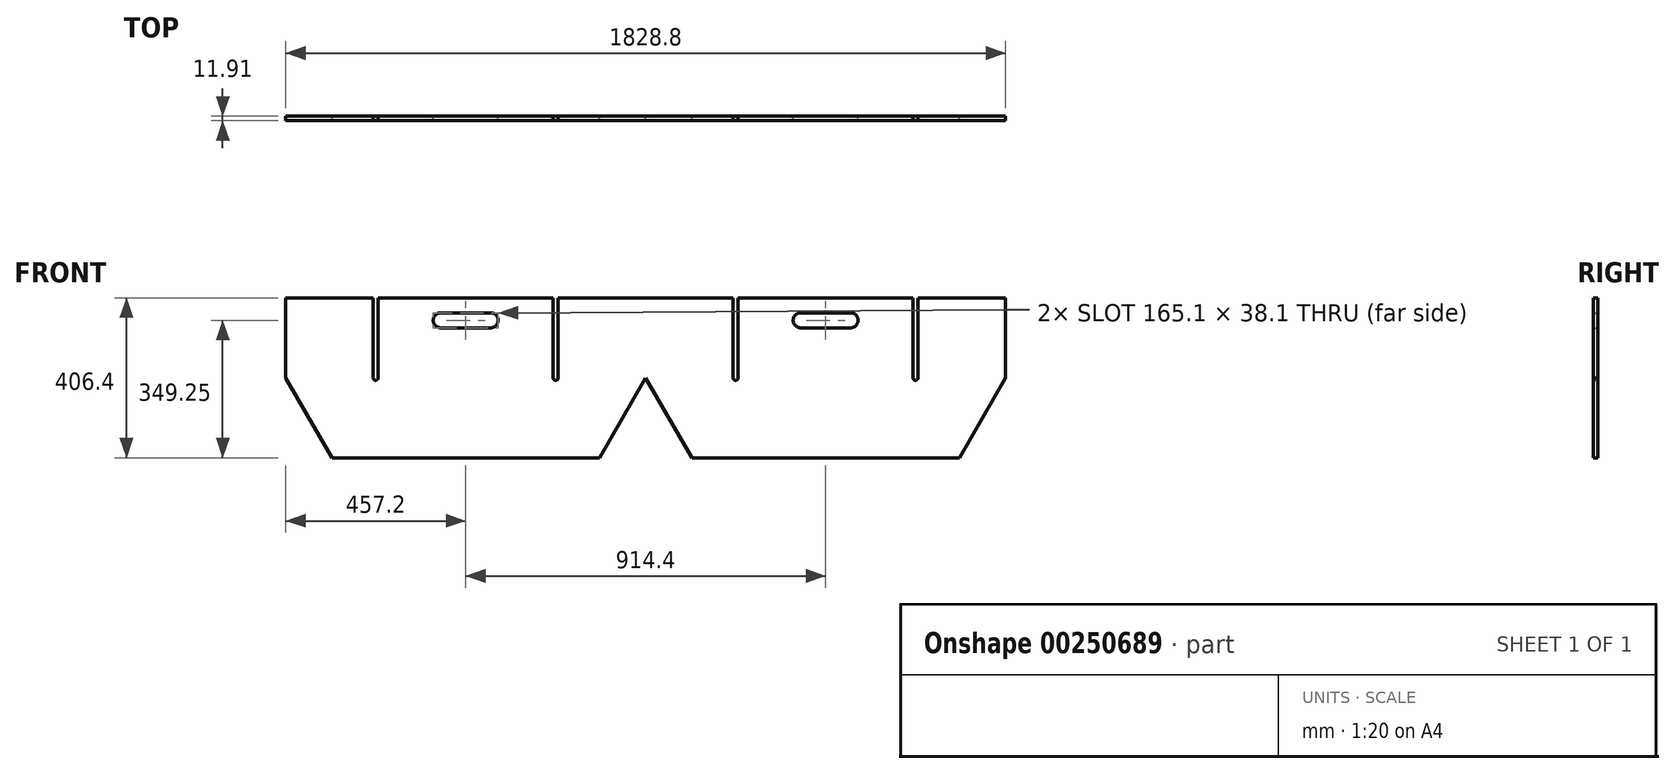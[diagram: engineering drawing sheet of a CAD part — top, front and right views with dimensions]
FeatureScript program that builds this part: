
annotation { "Feature Type Name" : "Feature", "Feature Type Description" : "" }
export const myFeature = defineFeature(function(context is Context, id is Id, definition is map)
    precondition{}
    {
        {
            var Q0;
            Q0=qCreatedBy(makeId("Front.planeOp"),FACE);
            var sketch = newSketch(context, id + "F0", { "sketchPlane" : qUnion([Q0])});
            skLineSegment(sketch, "E0.bottom", {"start": v(117.32, 0) * mm, "end": v(797.08, 0) * mm});
            skLineSegment(sketch, "E0.top", {"start": v(0, 406.4) * mm, "end": v(222.25, 406.4) * mm});
            skLineSegment(sketch, "E0.left", {"start": v(0, 203.2) * mm, "end": v(0, 406.4) * mm});
            skLineSegment(sketch, "E0.right", {"start": v(914.4, 0) * mm, "end": v(914.4, 406.4) * mm, "construction": true});
            skLineSegment(sketch, "E1", {"start": v(0, 203.2) * mm, "end": v(117.32, 0) * mm});
            skLineSegment(sketch, "E2", {"start": v(914.4, 203.2) * mm, "end": v(797.08, 0) * mm});
            skPoint(sketch, "E3.orphan", {"position": v(0, 0) * mm});
            skPoint(sketch, "E4", {"position": v(228.6, 406.4) * mm});
            skPoint(sketch, "E5", {"position": v(685.8, 406.4) * mm});
            skLineSegment(sketch, "E6", {"start": v(228.6, 406.4) * mm, "end": v(228.6, 203.2) * mm, "construction": true});
            skLineSegment(sketch, "E7", {"start": v(685.8, 406.4) * mm, "end": v(685.8, 203.2) * mm, "construction": true});
            skArc(sketch, "E8", {"start": v(222.25, 203.2) * mm, "mid": v(228.6, 196.85) * mm, "end": v(234.95, 203.2) * mm});
            skArc(sketch, "E9", {"start": v(679.45, 203.2) * mm, "mid": v(686.64, 196.9) * mm, "end": v(691.93, 204.87) * mm});
            skLineSegment(sketch, "E10", {"start": v(222.25, 203.2) * mm, "end": v(222.25, 406.4) * mm});
            skLineSegment(sketch, "E11", {"start": v(234.95, 203.2) * mm, "end": v(234.95, 406.4) * mm});
            skLineSegment(sketch, "E12", {"start": v(679.45, 203.2) * mm, "end": v(679.45, 406.4) * mm});
            skLineSegment(sketch, "E13", {"start": v(691.93, 204.87) * mm, "end": v(691.93, 406.4) * mm});
            skLineSegment(sketch, "E14.trimOffspring", {"start": v(691.93, 406.4) * mm, "end": v(914.4, 406.4) * mm});
            skLineSegment(sketch, "E15.trimOffspring", {"start": v(234.95, 406.4) * mm, "end": v(679.45, 406.4) * mm});
            skLineSegment(sketch, "E16", {"start": v(457.2, 406.4) * mm, "end": v(457.2, 368.3) * mm, "construction": true});
            skLineSegment(sketch, "E17", {"start": v(457.2, 368.3) * mm, "end": v(457.2, 330.2) * mm, "construction": true});
            skLineSegment(sketch, "E18", {"start": v(457.2, 368.3) * mm, "end": v(393.7, 368.3) * mm});
            skLineSegment(sketch, "E19", {"start": v(457.2, 330.2) * mm, "end": v(393.7, 330.2) * mm});
            skArc(sketch, "E20", {"start": v(393.7, 368.3) * mm, "mid": v(374.65, 349.25) * mm, "end": v(393.7, 330.2) * mm});
            skLineSegment(sketch, "E21.MirrorCS", {"start": v(457.2, 330.2) * mm, "end": v(520.7, 330.2) * mm});
            skArc(sketch, "E22.MirrorCS", {"start": v(520.7, 368.3) * mm, "mid": v(539.75, 349.25) * mm, "end": v(520.7, 330.2) * mm});
            skLineSegment(sketch, "E23.MirrorCS", {"start": v(457.2, 368.3) * mm, "end": v(520.7, 368.3) * mm});
            skArc(sketch, "E24.MirrorCS", {"start": v(1606.55, 203.2) * mm, "mid": v(1600.2, 196.85) * mm, "end": v(1593.85, 203.2) * mm});
            skArc(sketch, "E25.MirrorCS", {"start": v(1149.35, 203.2) * mm, "mid": v(1142.16, 196.9) * mm, "end": v(1136.87, 204.87) * mm});
            skLineSegment(sketch, "E26.MirrorCS", {"start": v(1371.6, 406.4) * mm, "end": v(1371.6, 368.3) * mm, "construction": true});
            skLineSegment(sketch, "E27.MirrorCS", {"start": v(1371.6, 368.3) * mm, "end": v(1435.1, 368.3) * mm});
            skLineSegment(sketch, "E28.MirrorCS", {"start": v(914.4, 203.2) * mm, "end": v(1031.72, 0) * mm});
            skPoint(sketch, "E29.MirrorP", {"position": v(1828.8, 0) * mm});
            skPoint(sketch, "E30.MirrorP", {"position": v(1143, 406.4) * mm});
            skLineSegment(sketch, "E31.MirrorCS", {"start": v(1828.8, 203.2) * mm, "end": v(1711.48, 0) * mm});
            skArc(sketch, "E32.MirrorCS", {"start": v(1308.1, 368.3) * mm, "mid": v(1289.05, 349.25) * mm, "end": v(1308.1, 330.2) * mm});
            skArc(sketch, "E33.MirrorCS", {"start": v(1435.1, 368.3) * mm, "mid": v(1454.15, 349.25) * mm, "end": v(1435.1, 330.2) * mm});
            skLineSegment(sketch, "E34.MirrorCS", {"start": v(1600.2, 406.4) * mm, "end": v(1600.2, 203.2) * mm, "construction": true});
            skPoint(sketch, "E35.MirrorP", {"position": v(1600.2, 406.4) * mm});
            skLineSegment(sketch, "E36.MirrorCS", {"start": v(1828.8, 406.4) * mm, "end": v(1606.55, 406.4) * mm});
            skLineSegment(sketch, "E37.MirrorCS", {"start": v(1711.48, 0) * mm, "end": v(1031.72, 0) * mm});
            skLineSegment(sketch, "E38.MirrorCS", {"start": v(1593.85, 203.2) * mm, "end": v(1593.85, 406.4) * mm});
            skLineSegment(sketch, "E39.MirrorCS", {"start": v(1143, 406.4) * mm, "end": v(1143, 203.2) * mm, "construction": true});
            skLineSegment(sketch, "E40.MirrorCS", {"start": v(1149.35, 203.2) * mm, "end": v(1149.35, 406.4) * mm});
            skLineSegment(sketch, "E41.MirrorCS", {"start": v(1828.8, 203.2) * mm, "end": v(1828.8, 406.4) * mm});
            skLineSegment(sketch, "E42.MirrorCS", {"start": v(1606.55, 203.2) * mm, "end": v(1606.55, 406.4) * mm});
            skLineSegment(sketch, "E43.MirrorCS", {"start": v(1371.6, 368.3) * mm, "end": v(1308.1, 368.3) * mm});
            skLineSegment(sketch, "E44.MirrorCS", {"start": v(1371.6, 330.2) * mm, "end": v(1308.1, 330.2) * mm});
            skLineSegment(sketch, "E45.MirrorCS", {"start": v(1593.85, 406.4) * mm, "end": v(1149.35, 406.4) * mm});
            skLineSegment(sketch, "E46.MirrorCS", {"start": v(1136.87, 406.4) * mm, "end": v(914.4, 406.4) * mm});
            skLineSegment(sketch, "E47.MirrorCS", {"start": v(1371.6, 368.3) * mm, "end": v(1371.6, 330.2) * mm, "construction": true});
            skLineSegment(sketch, "E48.MirrorCS", {"start": v(1136.87, 204.87) * mm, "end": v(1136.87, 406.4) * mm});
            skLineSegment(sketch, "E49.MirrorCS", {"start": v(1371.6, 330.2) * mm, "end": v(1435.1, 330.2) * mm});
            skSolve(sketch);
        }
        {
            var Q0;
            Q0=makeQuery(id+"F0.imprint","IMPRINT",FACE,{"disambiguationData":[TD([[makeQuery(id+"F0.imprint","IMPRINT",EDGE,{"derivedFrom":sQuery(id+"F0.wireOp",EDGE,"E0.bottom")}),1.0]])]});
            extrude(context, id + "F1", {"entities" : qUnion([Q0]), "depth" : 11.9 * mm});
        }
    });
